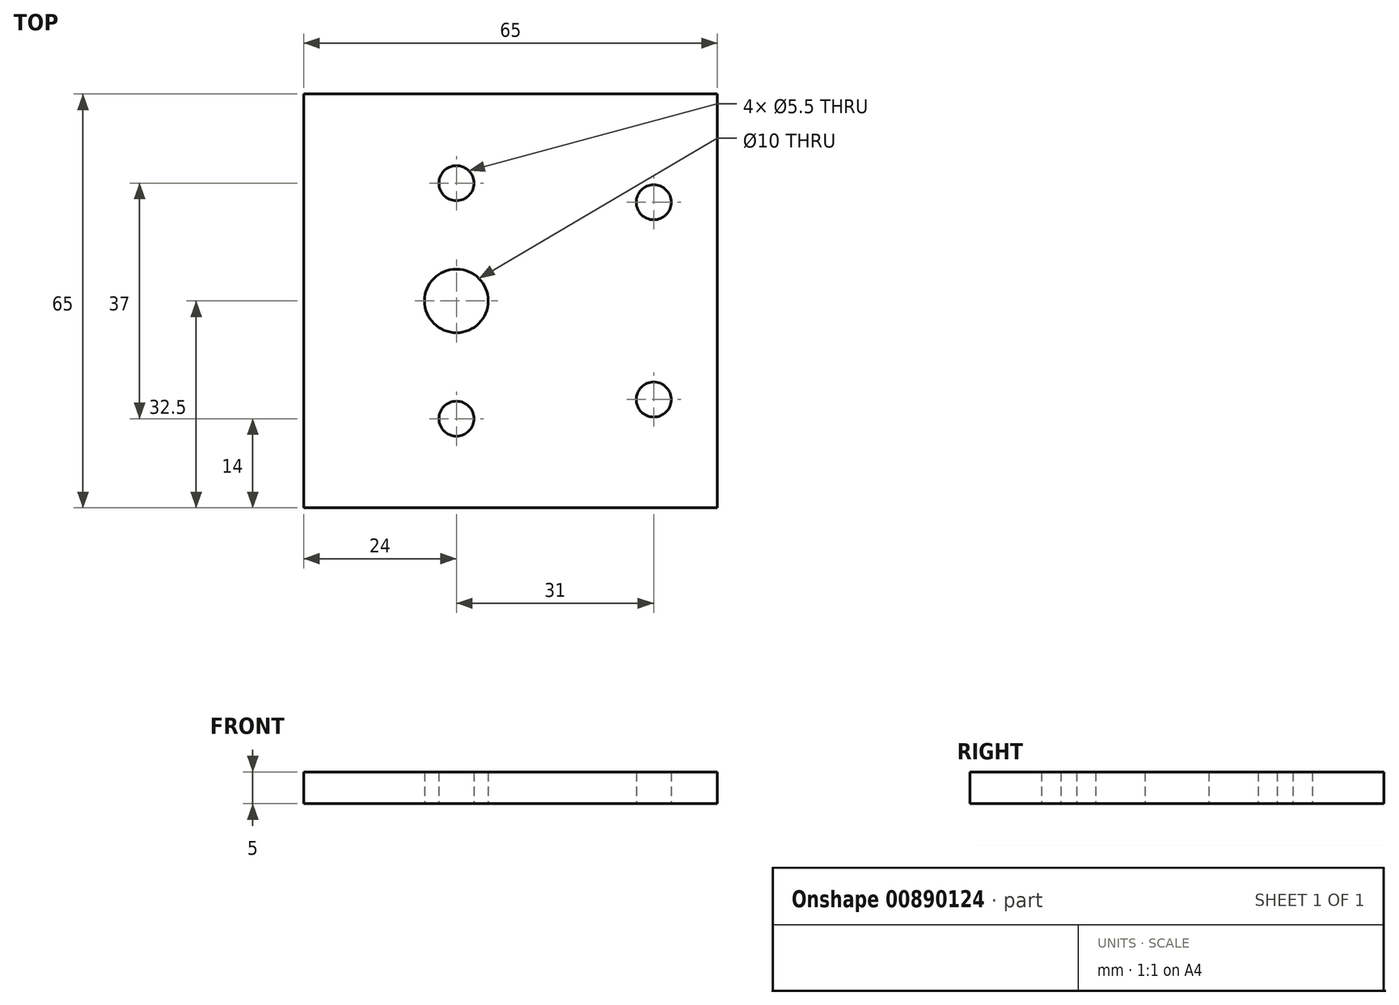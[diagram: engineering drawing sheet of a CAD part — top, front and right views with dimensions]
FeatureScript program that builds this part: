
annotation { "Feature Type Name" : "Feature", "Feature Type Description" : "" }
export const myFeature = defineFeature(function(context is Context, id is Id, definition is map)
    precondition{}
    {
        {
            var Q0;
            Q0=qCreatedBy(makeId("Front.planeOp"),FACE);
            var sketch = newSketch(context, id + "F0", { "sketchPlane" : qUnion([Q0])});
            skLineSegment(sketch, "E0.bottom", {"start": v(0, 0) * mm, "end": v(-65, 0) * mm});
            skLineSegment(sketch, "E0.top", {"start": v(0, 5) * mm, "end": v(-65, 5) * mm});
            skLineSegment(sketch, "E0.left", {"start": v(0, 0) * mm, "end": v(0, 5) * mm});
            skLineSegment(sketch, "E0.right", {"start": v(-65, 0) * mm, "end": v(-65, 5) * mm});
            skSolve(sketch);
        }
        {
            var Q0;
            Q0=qSketchRegion(id+"F0",true);
            extrude(context, id + "F1", {"entities" : qUnion([Q0]), "oppositeDirection" : true, "depth" : 65 * mm, "offsetDistance" : 25 * mm});
        }
        {
            var Q0;
            Q0=qCreatedBy(makeId("Top.planeOp"),FACE);
            var sketch = newSketch(context, id + "F2", { "sketchPlane" : qUnion([Q0])});
            skCircle(sketch, "E1", {"center": v(-10, 48) * mm, "radius": 2.75 * mm});
            skCircle(sketch, "E2", {"center": v(-10, 17) * mm, "radius": 2.75 * mm});
            skCircle(sketch, "E3", {"center": v(-41, 51) * mm, "radius": 2.75 * mm});
            skCircle(sketch, "E4", {"center": v(-41, 14) * mm, "radius": 2.75 * mm});
            skCircle(sketch, "E5", {"center": v(-41, 32.5) * mm, "radius": 5 * mm});
            skSolve(sketch);
        }
        {
            var Q0;
            Q0=qSketchRegion(id+"F2",true);
            extrude(context, id + "F3", {"entities" : qUnion([Q0]), "operationType" : NewBodyOperationType.REMOVE, "depth" : 5 * mm, "offsetDistance" : 25 * mm});
        }
    });
